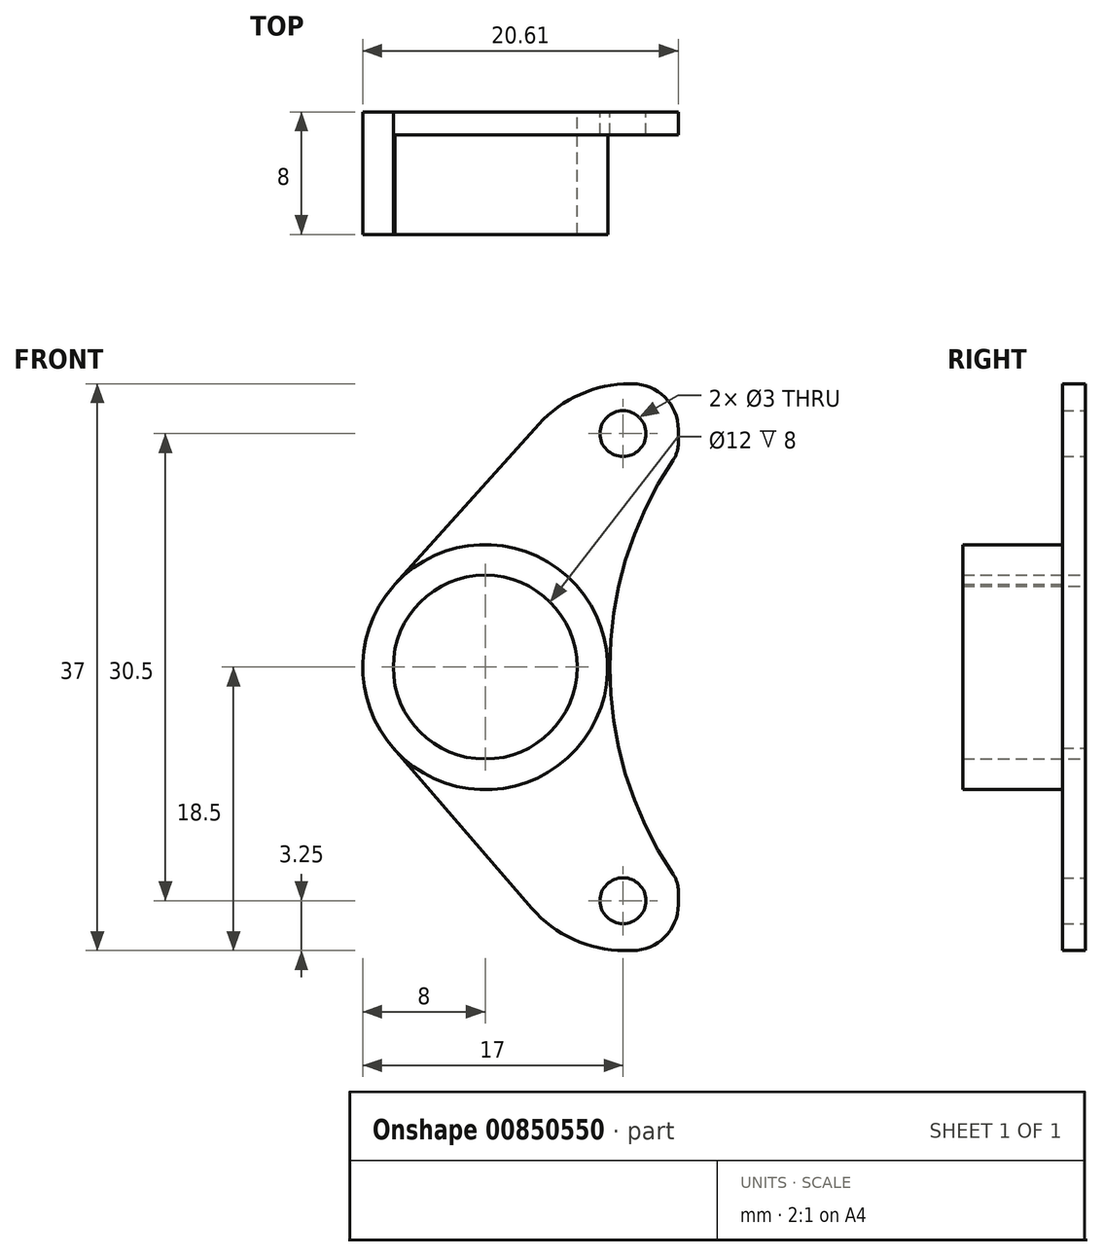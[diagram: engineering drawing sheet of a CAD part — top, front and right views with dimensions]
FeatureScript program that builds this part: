
annotation { "Feature Type Name" : "Feature", "Feature Type Description" : "" }
export const myFeature = defineFeature(function(context is Context, id is Id, definition is map)
    precondition{}
    {
        {
            var Q0;
            Q0=qCreatedBy(makeId("Front.planeOp"),FACE);
            var sketch = newSketch(context, id + "F0", { "sketchPlane" : qUnion([Q0])});
            skLineSegment(sketch, "E0.bottom", {"start": v(10.96, -18.5) * mm, "end": v(-26.06, -18.5) * mm});
            skLineSegment(sketch, "E0.top", {"start": v(11, 18.5) * mm, "end": v(-25.6, 18.5) * mm});
            skLineSegment(sketch, "E0.left", {"start": v(37.5, -10) * mm, "end": v(37.5, -6) * mm});
            skLineSegment(sketch, "E0.right", {"start": v(-37.5, -5.3) * mm, "end": v(-37.5, 5.3) * mm});
            skPoint(sketch, "E0.middle", {"position": v(0, 0) * mm});
            skPoint(sketch, "E1", {"position": v(-22.5, 15.25) * mm});
            skPoint(sketch, "E2", {"position": v(-22.5, -15.25) * mm});
            skPoint(sketch, "E3", {"position": v(8, 15.25) * mm});
            skPoint(sketch, "E4", {"position": v(8, -15.25) * mm});
            skPoint(sketch, "E5", {"position": v(35, 8.5) * mm});
            skPoint(sketch, "E6", {"position": v(35, -8.5) * mm});
            skCircle(sketch, "E7", {"center": v(-31.5, 0) * mm, "radius": 6 * mm});
            skCircle(sketch, "E8", {"center": v(-22.5, 15.25) * mm, "radius": 1.5 * mm});
            skCircle(sketch, "E9", {"center": v(-22.5, -15.25) * mm, "radius": 1.5 * mm});
            skCircle(sketch, "E10", {"center": v(8, 15.25) * mm, "radius": 1.5 * mm});
            skCircle(sketch, "E11", {"center": v(8, -15.25) * mm, "radius": 1.5 * mm});
            skCircle(sketch, "E12", {"center": v(35, 8.5) * mm, "radius": 1 * mm});
            skCircle(sketch, "E13", {"center": v(35, -8.5) * mm, "radius": 1 * mm});
            skCircle(sketch, "E14", {"center": v(-31.5, 0) * mm, "radius": 8 * mm});
            skLineSegment(sketch, "E15", {"start": v(-25.6, 18.5) * mm, "end": v(-37.5, 5.3) * mm});
            skLineSegment(sketch, "E16", {"start": v(-26.06, -18.5) * mm, "end": v(-37.5, -5.3) * mm});
            skPoint(sketch, "E17.orphan", {"position": v(-37.5, 18.5) * mm});
            skPoint(sketch, "E18.orphan", {"position": v(-37.5, -18.5) * mm});
            skPoint(sketch, "E19", {"position": v(37.5, -10) * mm});
            skPoint(sketch, "E20", {"position": v(37.5, 10) * mm});
            skLineSegment(sketch, "E21", {"start": v(11, 18.5) * mm, "end": v(37.5, 10) * mm});
            skLineSegment(sketch, "E22", {"start": v(10.96, -18.5) * mm, "end": v(37.5, -10) * mm});
            skPoint(sketch, "E23.orphan", {"position": v(37.5, 18.5) * mm});
            skPoint(sketch, "E24.orphan", {"position": v(37.5, -18.5) * mm});
            skPoint(sketch, "E25", {"position": v(37.5, 6) * mm});
            skPoint(sketch, "E26", {"position": v(37.5, -6) * mm});
            skLineSegment(sketch, "E27", {"start": v(37.5, 6) * mm, "end": v(23.9, 6) * mm});
            skLineSegment(sketch, "E28", {"start": v(37.5, -6) * mm, "end": v(23.9, -6) * mm});
            skArc(sketch, "E29", {"start": v(23.9, 6) * mm, "mid": v(17.9, 0) * mm, "end": v(23.9, -6) * mm});
            skLineSegment(sketch, "E30.trimOffspring", {"start": v(37.5, 6) * mm, "end": v(37.5, 10) * mm});
            skLineSegment(sketch, "E31", {"start": v(-18.89, 18.5) * mm, "end": v(-18.89, -18.5) * mm});
            skPoint(sketch, "E32", {"position": v(-18.89, 14) * mm});
            skPoint(sketch, "E33", {"position": v(-18.89, -14) * mm});
            skArc(sketch, "E34", {"start": v(-18.89, 14) * mm, "mid": v(-23.37, 0) * mm, "end": v(-18.89, -14) * mm});
            skSolve(sketch);
        }
        {
            var Q0;
            Q0=makeQuery(id+"F0.imprint","IMPRINT",FACE,{"disambiguationData":[TD([[makeQuery(id+"F0.imprint","IMPRINT",EDGE,{"derivedFrom":sQuery(id+"F0.wireOp",EDGE,"E8")}),-1.0]])]});
            extrude(context, id + "F1", {"entities" : qUnion([Q0]), "depth" : 1.5 * mm, "offsetDistance" : 25 * mm});
        }
        {
            var Q0;
            {var subQ0=sQuery(id+"F0.wireOp",EDGE,"E7");Q0=makeQuery(id+"F0.imprint","IMPRINT",FACE,{"disambiguationData":[TD([[makeQuery(id+"F0.imprint","IMPRINT",EDGE,{"derivedFrom":subQ0}),-1.0]])]});}
            var Q1;
            {var subQ0=sQuery(id+"F0.wireOp",EDGE,"E14");var subQ1=sQuery(id+"F0.wireOp",EDGE,"E0.right");var subQ2=makeQuery(id+"F0.imprint","INTERSECT",VERTEX,{"derivedFrom":[subQ1,subQ0]});Q1=makeQuery(id+"F0.imprint","IMPRINT",FACE,{"disambiguationData":[TD([[makeQuery(id+"F0.imprint","IMPRINT",EDGE,{"disambiguationData":[TD([[subQ2,-1.0]])],"derivedFrom":subQ1}),1.0]])]});}
            extrude(context, id + "F2", {"entities" : qUnion([Q0, Q1]), "operationType" : NewBodyOperationType.ADD, "depth" : 8 * mm, "offsetDistance" : 25 * mm});
        }
        {
            var Q0;
            Q0=makeQuery(id+"F1.opExtrude","SWEPT_EDGE",EDGE,{"disambiguationData":[OSD([sQuery(id+"F0.wireOp",EDGE,"E0.bottom"),sQuery(id+"F0.wireOp",EDGE,"E16")])]});
            fillet(context, id + "F3", {"entities" : qUnion([Q0]), "radius" : 8 * mm, "tangentPropagation" : true, "allowEdgeOverflow" : false});
        }
        {
            var Q0;
            Q0=makeQuery(id+"F1.opExtrude","SWEPT_EDGE",EDGE,{"disambiguationData":[OSD([sQuery(id+"F0.wireOp",EDGE,"E0.bottom"),sQuery(id+"F0.wireOp",EDGE,"E31")])]});
            fillet(context, id + "F4", {"entities" : qUnion([Q0]), "radius" : 3 * mm, "tangentPropagation" : true, "allowEdgeOverflow" : false});
        }
        {
            var Q0;
            {var subQ0=sQuery(id+"F0.wireOp",EDGE,"E34");var subQ1=sQuery(id+"F0.wireOp",EDGE,"E31");Q0=makeQuery(id+"F1.opExtrude","SWEPT_EDGE",EDGE,{"disambiguationData":[OSD([subQ1,subQ0]),TDD([makeQuery(id+"F0.imprint","INTERSECT",VERTEX,{"disambiguationData":[OD(1.0)],"derivedFrom":[subQ1,subQ0]})])]});}
            fillet(context, id + "F5", {"entities" : qUnion([Q0]), "radius" : 2 * mm, "tangentPropagation" : true, "allowEdgeOverflow" : false});
        }
        {
            var Q0;
            Q0=makeQuery(id+"F1.opExtrude","SWEPT_EDGE",EDGE,{"disambiguationData":[OSD([sQuery(id+"F0.wireOp",EDGE,"E0.top"),sQuery(id+"F0.wireOp",EDGE,"E15")])]});
            fillet(context, id + "F6", {"entities" : qUnion([Q0]), "radius" : 8 * mm, "tangentPropagation" : true, "allowEdgeOverflow" : false});
        }
        {
            var Q0;
            Q0=makeQuery(id+"F1.opExtrude","SWEPT_EDGE",EDGE,{"disambiguationData":[OSD([sQuery(id+"F0.wireOp",EDGE,"E0.top"),sQuery(id+"F0.wireOp",EDGE,"E31")])]});
            fillet(context, id + "F7", {"entities" : qUnion([Q0]), "radius" : 3 * mm, "tangentPropagation" : true, "allowEdgeOverflow" : false});
        }
        {
            var Q0;
            {var subQ0=sQuery(id+"F0.wireOp",EDGE,"E34");var subQ1=sQuery(id+"F0.wireOp",EDGE,"E31");Q0=makeQuery(id+"F1.opExtrude","SWEPT_EDGE",EDGE,{"disambiguationData":[OSD([subQ1,subQ0]),TDD([makeQuery(id+"F0.imprint","INTERSECT",VERTEX,{"disambiguationData":[OD(0.0)],"derivedFrom":[subQ1,subQ0]})])]});}
            fillet(context, id + "F8", {"entities" : qUnion([Q0]), "radius" : 2 * mm, "tangentPropagation" : true, "allowEdgeOverflow" : false});
        }
    });
